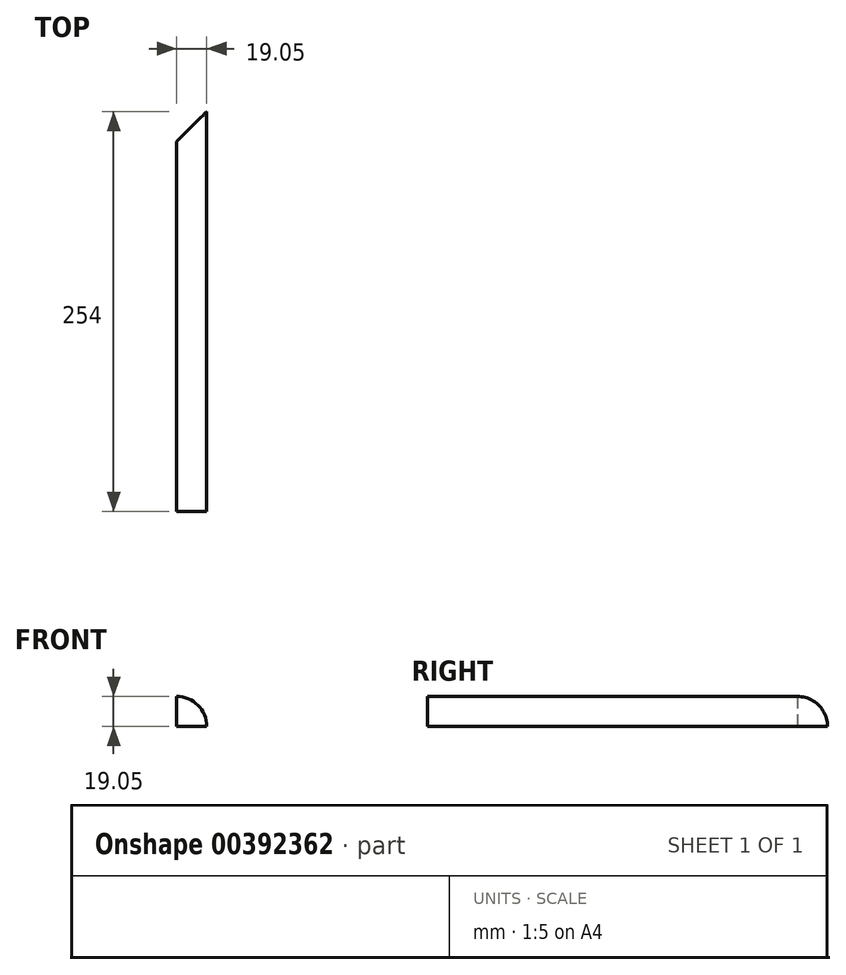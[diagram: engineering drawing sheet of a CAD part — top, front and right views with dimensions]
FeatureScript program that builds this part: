
annotation { "Feature Type Name" : "Feature", "Feature Type Description" : "" }
export const myFeature = defineFeature(function(context is Context, id is Id, definition is map)
    precondition{}
    {
        {
            var Q0;
            Q0=qCreatedBy(makeId("Front.planeOp"),FACE);
            var sketch = newSketch(context, id + "F0", { "sketchPlane" : qUnion([Q0])});
            skLineSegment(sketch, "E0.bottom", {"start": v(0, 0) * mm, "end": v(19.05, 0) * mm});
            skLineSegment(sketch, "E0.left", {"start": v(0, 0) * mm, "end": v(0, 19.05) * mm});
            skArc(sketch, "E1", {"start": v(19.05, 0) * mm, "mid": v(13.47, 13.47) * mm, "end": v(0, 19.05) * mm});
            skSolve(sketch);
        }
        {
            var Q0;
            Q0=makeQuery(id+"F0.imprint","IMPRINT",FACE,{"disambiguationData":[TD([[makeQuery(id+"F0.imprint","IMPRINT",EDGE,{"derivedFrom":sQuery(id+"F0.wireOp",EDGE,"E0.bottom")}),1.0]])]});
            extrude(context, id + "F1", {"entities" : qUnion([Q0]), "depth" : 254 * mm});
        }
        {
            var Q0;
            Q0=makeQuery(id+"F1.opExtrude","SWEPT_FACE",FACE,{"disambiguationData":[OSD([sQuery(id+"F0.wireOp",EDGE,"E0.bottom")])]});
            var sketch = newSketch(context, id + "F2", { "sketchPlane" : qUnion([Q0])});
            skLineSegment(sketch, "E2", {"start": v(19.05, 0) * mm, "end": v(0, 19.05) * mm});
            skSolve(sketch);
        }
        {
            var Q0;
            {var subQ0=sQuery(id+"F2.wireOp",EDGE,"E2");Q0=makeQuery(id+"F2.imprint","IMPRINT",FACE,{"disambiguationData":[TD([[makeQuery(id+"F2.imprint","IMPRINT",EDGE,{"derivedFrom":subQ0}),1.0]])]});}
            extrude(context, id + "F3", {"entities" : qUnion([Q0]), "operationType" : NewBodyOperationType.REMOVE, "oppositeDirection" : true, "depth" : 25.4 * mm});
        }
    });
